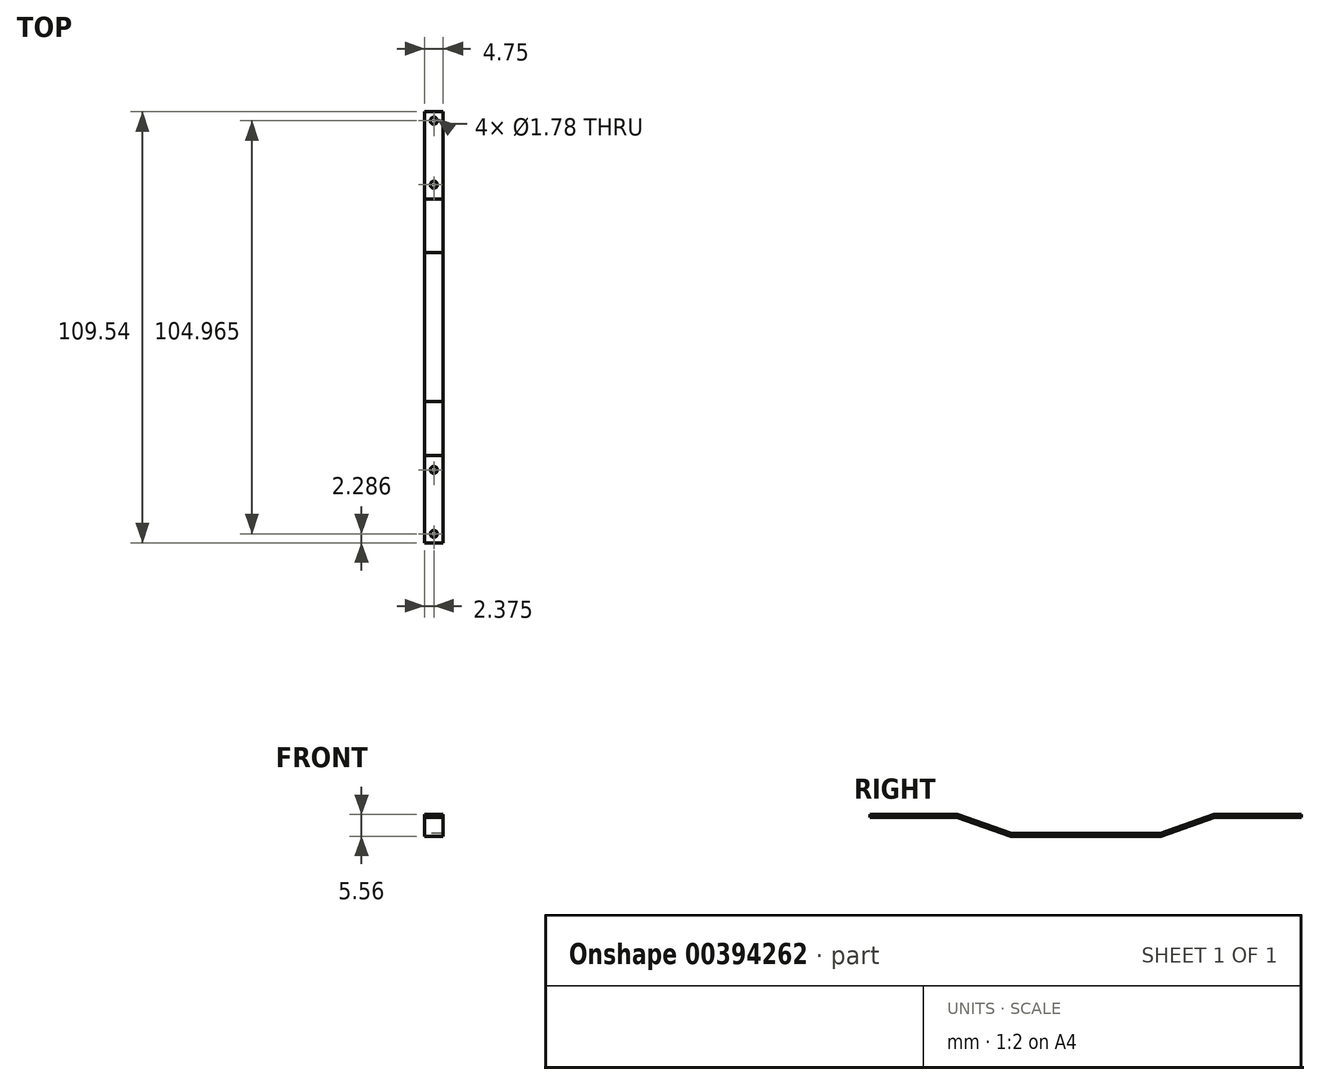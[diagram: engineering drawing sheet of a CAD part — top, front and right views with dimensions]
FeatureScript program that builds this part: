
annotation { "Feature Type Name" : "Feature", "Feature Type Description" : "" }
export const myFeature = defineFeature(function(context is Context, id is Id, definition is map)
    precondition{}
    {
        {
            var Q0;
            Q0=qCreatedBy(makeId("Right.planeOp"),FACE);
            var sketch = newSketch(context, id + "F0", { "sketchPlane" : qUnion([Q0])});
            skLineSegment(sketch, "E0.bottom", {"start": v(35.72, 0) * mm, "end": v(73.82, 0) * mm});
            skLineSegment(sketch, "E0.top", {"start": v(0, 5.56) * mm, "end": v(22.23, 5.56) * mm});
            skLineSegment(sketch, "E0.left", {"start": v(0, 4.77) * mm, "end": v(0, 5.56) * mm});
            skLineSegment(sketch, "E1", {"start": v(22.23, 5.56) * mm, "end": v(35.85, 0.79) * mm});
            skLineSegment(sketch, "E2", {"start": v(87.31, 5.56) * mm, "end": v(73.69, 0.79) * mm});
            skLineSegment(sketch, "E3", {"start": v(0, 4.77) * mm, "end": v(22.1, 4.77) * mm});
            skLineSegment(sketch, "E4", {"start": v(35.85, 0.79) * mm, "end": v(73.69, 0.79) * mm});
            skLineSegment(sketch, "E5", {"start": v(73.82, 0) * mm, "end": v(87.45, 4.77) * mm});
            skLineSegment(sketch, "E6", {"start": v(35.72, 0) * mm, "end": v(22.1, 4.77) * mm});
            skLineSegment(sketch, "E7.trimOffspring", {"start": v(87.31, 5.56) * mm, "end": v(109.54, 5.56) * mm});
            skLineSegment(sketch, "E8.trimOffspring", {"start": v(87.45, 4.77) * mm, "end": v(109.54, 4.77) * mm});
            skPoint(sketch, "E9.orphan", {"position": v(38.1, 0) * mm});
            skPoint(sketch, "E10.visualSharp", {"position": v(22.1, 4.77) * mm});
            skLineSegment(sketch, "E10.filletArc", {"start": v(22.1, 4.77) * mm, "end": v(22.1, 4.77) * mm});
            skPoint(sketch, "E11.visualSharp", {"position": v(22.23, 5.56) * mm});
            skLineSegment(sketch, "E11.filletArc", {"start": v(22.23, 5.56) * mm, "end": v(22.23, 5.56) * mm});
            skPoint(sketch, "E12.visualSharp", {"position": v(35.72, 0) * mm});
            skLineSegment(sketch, "E12.filletArc", {"start": v(35.72, 0) * mm, "end": v(35.72, 0) * mm});
            skPoint(sketch, "E13.visualSharp", {"position": v(73.82, 0) * mm});
            skLineSegment(sketch, "E13.filletArc", {"start": v(73.82, 0) * mm, "end": v(73.82, 0) * mm});
            skPoint(sketch, "E14.visualSharp", {"position": v(87.31, 5.56) * mm});
            skLineSegment(sketch, "E14.filletArc", {"start": v(87.31, 5.56) * mm, "end": v(87.31, 5.56) * mm});
            skPoint(sketch, "E15.visualSharp", {"position": v(87.45, 4.77) * mm});
            skPoint(sketch, "E16.visualSharp", {"position": v(35.85, 0.79) * mm});
            skLineSegment(sketch, "E17", {"start": v(73.69, 0.79) * mm, "end": v(74.2, 0.97) * mm});
            skLineSegment(sketch, "E18", {"start": v(73.69, 0.79) * mm, "end": v(73.15, 0.79) * mm});
            skLineSegment(sketch, "E19", {"start": v(109.54, 4.77) * mm, "end": v(109.54, 5.56) * mm});
            skPoint(sketch, "E20.orphan", {"position": v(0, 0) * mm});
            skSolve(sketch);
        }
        {
            var Q0;
            Q0=makeQuery(id+"F0.imprint","IMPRINT",FACE,{"disambiguationData":[TD([[makeQuery(id+"F0.imprint","IMPRINT",EDGE,{"derivedFrom":sQuery(id+"F0.wireOp",EDGE,"E0.bottom")}),1.0]])]});
            extrude(context, id + "F1", {"entities" : qUnion([Q0]), "depth" : 4.75 * mm});
        }
        {
            var Q0;
            Q0=makeQuery(id+"F1.opExtrude","SWEPT_FACE",FACE,{"disambiguationData":[OSD([sQuery(id+"F0.wireOp",EDGE,"E7.trimOffspring")])]});
            var sketch = newSketch(context, id + "F2", { "sketchPlane" : qUnion([Q0])});
            skLineSegment(sketch, "E21", {"start": v(2.37, 87.31) * mm, "end": v(2.37, 0) * mm, "construction": true});
            skCircle(sketch, "E22", {"center": v(2.37, 2.29) * mm, "radius": 0.89 * mm});
            skCircle(sketch, "E23", {"center": v(2.37, 107.25) * mm, "radius": 0.89 * mm});
            skCircle(sketch, "E24", {"center": v(2.37, 91) * mm, "radius": 0.89 * mm});
            skCircle(sketch, "E25", {"center": v(2.37, 18.54) * mm, "radius": 0.89 * mm});
            skSolve(sketch);
        }
        {
            var Q0;
            Q0 = qSketchRegion(id + "F2", true);
            extrude(context, id + "F3", {"entities" : qUnion([Q0]), "operationType" : NewBodyOperationType.REMOVE, "endBound" : BoundingType.UP_TO_NEXT, "oppositeDirection" : true, "depth" : 25.4 * mm, "hasSecondDirection" : true, "secondDirectionOppositeDirection" : false, "secondDirectionDepth" : 25.4 * mm});
        }
    });
